annotation { "Feature Type Name" : "Feature", "Feature Type Description" : "" }
export const myFeature = defineFeature(function(context is Context, id is Id, definition is map)
    precondition{}
    {
        {
            var Q0;
            Q0=qCreatedBy(makeId("Top.planeOp"),FACE);
            var sketch = newSketch(context, id + "F0", { "sketchPlane" : qUnion([Q0])});
            skLineSegment(sketch, "E0.bottom", {"start": v(-51.86, 92.51) * mm, "end": v(-32.8, 92.51) * mm});
            skLineSegment(sketch, "E0.top", {"start": v(-51.86, -110.69) * mm, "end": v(-32.8, -110.69) * mm});
            skLineSegment(sketch, "E0.left", {"start": v(-51.86, 92.51) * mm, "end": v(-51.86, -110.69) * mm});
            skLineSegment(sketch, "E0.right", {"start": v(-32.8, 92.51) * mm, "end": v(-32.8, -110.69) * mm});
            skCircle(sketch, "E1", {"center": v(-42.33, 116.06) * mm, "radius": 25.4 * mm});
            skPoint(sketch, "E1.third.point", {"position": v(-42.33, 141.46) * mm});
            skPoint(sketch, "E1.third.point.positionSnap0", {"position": v(-42.33, 92.51) * mm});
            skCircle(sketch, "E2", {"center": v(-42.33, 116.06) * mm, "radius": 19.05 * mm});
            skLineSegment(sketch, "E3", {"start": v(-42.33, -110.69) * mm, "end": v(-32.8, -60.79) * mm});
            skLineSegment(sketch, "E4", {"start": v(-42.33, -110.69) * mm, "end": v(-51.86, -60.79) * mm});
            skSolve(sketch);
        }
        {
            var Q0;
            {var subQ6=sQuery(id+"F0.wireOp",EDGE,"E3");Q0=makeQuery(id+"F0.imprint","IMPRINT",FACE,{"disambiguationData":[TD([[makeQuery(id+"F0.imprint","IMPRINT",EDGE,{"derivedFrom":subQ6}),1.0]])]});}
            var Q1;
            {var subQ0=sQuery(id+"F0.wireOp",EDGE,"E0.bottom");Q1=makeQuery(id+"F0.imprint","IMPRINT",FACE,{"disambiguationData":[TD([[makeQuery(id+"F0.imprint","IMPRINT",EDGE,{"derivedFrom":subQ0}),-1.0]])]});}
            var Q2;
            {var subQ0=sQuery(id+"F0.wireOp",EDGE,"E0.bottom");Q2=makeQuery(id+"F0.imprint","IMPRINT",FACE,{"disambiguationData":[TD([[makeQuery(id+"F0.imprint","IMPRINT",EDGE,{"derivedFrom":subQ0}),1.0]])]});}
            extrude(context, id + "F1", {"entities" : qUnion([Q0, Q1, Q2]), "depth" : 3.17 * mm, "offsetDistance" : 25.4 * mm});
        }
        {
            var Q0;
            Q0=makeQuery(id+"F1.opExtrude","CAP_FACE",FACE,{"disambiguationData":[OSD([sQuery(id+"F0.wireOp",EDGE,"E0.left"),sQuery(id+"F0.wireOp",EDGE,"E0.right"),sQuery(id+"F0.wireOp",EDGE,"E1"),sQuery(id+"F0.wireOp",EDGE,"E2"),sQuery(id+"F0.wireOp",EDGE,"E3"),sQuery(id+"F0.wireOp",EDGE,"E4")])],"isStart":false});
            var sketch = newSketch(context, id + "F2", { "sketchPlane" : qUnion([Q0])});
            skLineSegment(sketch, "E5", {"start": v(-51.86, -60.79) * mm, "end": v(-32.8, -60.79) * mm});
            skLineSegment(sketch, "E6", {"start": v(-42.33, -110.69) * mm, "end": v(-43.92, -60.79) * mm});
            skLineSegment(sketch, "E7", {"start": v(-42.33, -110.69) * mm, "end": v(-40.74, -60.79) * mm});
            skPoint(sketch, "E8", {"position": v(-42.33, -60.79) * mm});
            skLineSegment(sketch, "E9", {"start": v(-51.86, 92.51) * mm, "end": v(-32.8, 92.51) * mm});
            skLineSegment(sketch, "E10.bottom", {"start": v(-43.92, -60.79) * mm, "end": v(-40.74, -60.79) * mm});
            skLineSegment(sketch, "E10.top", {"start": v(-43.92, 92.51) * mm, "end": v(-40.74, 92.51) * mm});
            skLineSegment(sketch, "E10.left", {"start": v(-43.92, -60.79) * mm, "end": v(-43.92, 92.51) * mm});
            skLineSegment(sketch, "E10.right", {"start": v(-40.74, -60.79) * mm, "end": v(-40.74, 92.51) * mm});
            skSolve(sketch);
        }
        {
            var Q0;
            Q0=makeQuery(id+"F2.imprint","IMPRINT",FACE,{"disambiguationData":[TD([[makeQuery(id+"F2.imprint","IMPRINT",EDGE,{"derivedFrom":sQuery(id+"F2.wireOp",EDGE,"E10.bottom")}),1.0]])]});
            var Q1;
            Q1=makeQuery(id+"F2.imprint","IMPRINT",FACE,{"disambiguationData":[TD([[makeQuery(id+"F2.imprint","IMPRINT",EDGE,{"derivedFrom":sQuery(id+"F2.wireOp",EDGE,"E6")}),-1.0]])]});
            extrude(context, id + "F3", {"entities" : qUnion([Q0, Q1]), "operationType" : NewBodyOperationType.ADD, "depth" : 12.7 * mm, "offsetDistance" : 25.4 * mm});
        }
        {
            var Q0;
            Q0=qCreatedBy(makeId("Right.planeOp"),FACE);
            var sketch = newSketch(context, id + "F4", { "sketchPlane" : qUnion([Q0])});
            skLineSegment(sketch, "E11.0.0", {"start": v(-60.79, 3.18) * mm, "end": v(92.51, 3.18) * mm});
            skLineSegment(sketch, "E11.0.1", {"start": v(92.51, 3.18) * mm, "end": v(92.51, 15.88) * mm});
            skLineSegment(sketch, "E11.0.2", {"start": v(92.51, 15.88) * mm, "end": v(-60.79, 15.88) * mm});
            skLineSegment(sketch, "E11.0.3", {"start": v(-60.79, 15.88) * mm, "end": v(-60.79, 3.18) * mm});
            skLineSegment(sketch, "E12.0.0", {"start": v(-110.69, 3.18) * mm, "end": v(-60.79, 3.18) * mm});
            skLineSegment(sketch, "E12.0.1", {"start": v(-60.79, 3.18) * mm, "end": v(-60.79, 15.88) * mm});
            skLineSegment(sketch, "E12.0.2", {"start": v(-60.79, 15.88) * mm, "end": v(-110.69, 15.88) * mm});
            skLineSegment(sketch, "E12.0.3", {"start": v(-110.69, 15.88) * mm, "end": v(-110.69, 3.18) * mm});
            skLineSegment(sketch, "E13", {"start": v(-60.79, 15.87) * mm, "end": v(-110.69, 3.17) * mm});
            skArc(sketch, "E14", {"start": v(92.51, 3.17) * mm, "mid": v(68.36, 12.43) * mm, "end": v(42.73, 15.87) * mm});
            skSolve(sketch);
        }
        {
            var Q0;
            Q0=makeQuery(id+"F4.imprint","IMPRINT",FACE,{"disambiguationData":[TD([[makeQuery(id+"F4.imprint","IMPRINT",EDGE,{"derivedFrom":sQuery(id+"F4.wireOp",EDGE,"E12.0.2")}),1.0]])]});
            var Q1;
            {var subQ0=sQuery(id+"F4.wireOp",EDGE,"E11.0.1");Q1=makeQuery(id+"F4.imprint","IMPRINT",FACE,{"disambiguationData":[TD([[makeQuery(id+"F4.imprint","IMPRINT",EDGE,{"derivedFrom":subQ0}),1.0]])]});}
            extrude(context, id + "F5", {"entities" : qUnion([Q0, Q1]), "operationType" : NewBodyOperationType.REMOVE, "oppositeDirection" : true, "depth" : 128.02 * mm, "offsetDistance" : 25.4 * mm});
        }
        {
            var Q0;
            Q0=makeQuery(id+"F1.opExtrude","CAP_FACE",FACE,{"disambiguationData":[OSD([sQuery(id+"F0.wireOp",EDGE,"E0.left"),sQuery(id+"F0.wireOp",EDGE,"E0.right"),sQuery(id+"F0.wireOp",EDGE,"E1"),sQuery(id+"F0.wireOp",EDGE,"E2"),sQuery(id+"F0.wireOp",EDGE,"E3"),sQuery(id+"F0.wireOp",EDGE,"E4")])],"isStart":true});
            var sketch = newSketch(context, id + "F6", { "sketchPlane" : qUnion([Q0])});
            skLineSegment(sketch, "E15.bottom", {"start": v(-20.1, -92.51) * mm, "end": v(-64.56, -92.51) * mm});
            skLineSegment(sketch, "E15.top", {"start": v(-20.1, -79.81) * mm, "end": v(-64.56, -79.81) * mm});
            skLineSegment(sketch, "E15.left", {"start": v(-20.1, -92.51) * mm, "end": v(-20.1, -79.81) * mm});
            skLineSegment(sketch, "E15.right", {"start": v(-64.56, -92.51) * mm, "end": v(-64.56, -79.81) * mm});
            skLineSegment(sketch, "E16.0.0", {"start": v(-32.8, -92.51) * mm, "end": v(-32.8, 60.79) * mm});
            skLineSegment(sketch, "E16.0.1", {"start": v(-32.8, 60.79) * mm, "end": v(-42.33, 110.69) * mm});
            skLineSegment(sketch, "E16.0.2", {"start": v(-42.33, 110.69) * mm, "end": v(-51.86, 60.79) * mm});
            skLineSegment(sketch, "E16.0.3", {"start": v(-51.86, 60.79) * mm, "end": v(-51.86, -92.51) * mm});
            skArc(sketch, "E16.0.4", {"start": v(-51.86, -92.51) * mm, "mid": v(-42.33, -141.46) * mm, "end": v(-32.8, -92.51) * mm});
            skSolve(sketch);
        }
        {
            var Q0;
            {var subQ3=sQuery(id+"F6.wireOp",EDGE,"E15.left");Q0=makeQuery(id+"F6.imprint","IMPRINT",FACE,{"disambiguationData":[TD([[makeQuery(id+"F6.imprint","IMPRINT",EDGE,{"derivedFrom":subQ3}),1.0]])]});}
            var Q1;
            {var subQ3=sQuery(id+"F6.wireOp",EDGE,"E15.right");Q1=makeQuery(id+"F6.imprint","IMPRINT",FACE,{"disambiguationData":[TD([[makeQuery(id+"F6.imprint","IMPRINT",EDGE,{"derivedFrom":subQ3}),-1.0]])]});}
            extrude(context, id + "F7", {"entities" : qUnion([Q0, Q1]), "operationType" : NewBodyOperationType.ADD, "oppositeDirection" : true, "depth" : 3.17 * mm, "offsetDistance" : 25.4 * mm});
        }
        {
            var Q0;
            Q0=makeQuery(id+"F1.opExtrude","SWEPT_BODY",BODY,{"disambiguationData":[OSD([sQuery(id+"F0.wireOp",EDGE,"E0.left"),sQuery(id+"F0.wireOp",EDGE,"E0.right"),sQuery(id+"F0.wireOp",EDGE,"E1"),sQuery(id+"F0.wireOp",EDGE,"E2"),sQuery(id+"F0.wireOp",EDGE,"E3"),sQuery(id+"F0.wireOp",EDGE,"E4")])]});
            var Q1;
            Q1=makeQuery(id+"F7.opExtrude","CAP_EDGE",EDGE,{"disambiguationData":[OSD([sQuery(id+"F6.wireOp",EDGE,"E15.left")])],"isStart":true});
            transform(context, id + "F8", {"entities" : qUnion([Q0]), "transformType" : TransformType.ROTATION, "transformAxis" : qUnion([Q1]), "angle" : 180 * degree, "makeCopy" : false});
        }
        {
            var Q0;
            {var subQ0=sQuery(id+"F6.wireOp",EDGE,"E15.top");var subQ1=sQuery(id+"F6.wireOp",EDGE,"E15.bottom");Q0=makeQuery(id+"F7.boolean.opBoolean","MERGE",FACE,{"derivedFrom":[makeQuery(id+"F1.opExtrude","CAP_FACE",FACE,{"disambiguationData":[OSD([sQuery(id+"F0.wireOp",EDGE,"E0.left"),sQuery(id+"F0.wireOp",EDGE,"E0.right"),sQuery(id+"F0.wireOp",EDGE,"E1"),sQuery(id+"F0.wireOp",EDGE,"E2"),sQuery(id+"F0.wireOp",EDGE,"E3"),sQuery(id+"F0.wireOp",EDGE,"E4")])],"isStart":true}),makeQuery(id+"F7.opExtrude","CAP_FACE",FACE,{"disambiguationData":[OSD([subQ1,subQ0,sQuery(id+"F6.wireOp",EDGE,"E15.left"),sQuery(id+"F6.wireOp",EDGE,"E16.0.0")])],"isStart":true}),makeQuery(id+"F7.opExtrude","CAP_FACE",FACE,{"disambiguationData":[OSD([subQ1,subQ0,sQuery(id+"F6.wireOp",EDGE,"E15.right"),sQuery(id+"F6.wireOp",EDGE,"E16.0.3")])],"isStart":true})]});}
            var sketch = newSketch(context, id + "F9", { "sketchPlane" : qUnion([Q0])});
            skText(sketch, "E17", { "text": "JMM BIO", "fontName": "OpenSans-Bold.ttf"});
            skPoint(sketch, "E18", {"position": v(-17.57, 89.97) * mm});
            const initialGuessF9  = {"E17": [-0.01757, 0.08347, 1, 0, 0.0065]};
            skSetInitialGuess(sketch, initialGuessF9);
            skSolve(sketch);
        }
        {
            var Q0;
            Q0=makeQuery(id+"F9.imprint","IMPRINT",FACE,{"disambiguationData":[TD([[makeQuery(id+"F9.imprint","IMPRINT",EDGE,{"derivedFrom":sQuery(id+"F9.wireOp",EDGE,"E17.sketch_text.stroke-0")}),-1.0]])]});
            var Q1;
            Q1=makeQuery(id+"F9.imprint","IMPRINT",FACE,{"disambiguationData":[TD([[makeQuery(id+"F9.imprint","IMPRINT",EDGE,{"derivedFrom":sQuery(id+"F9.wireOp",EDGE,"E17.sketch_text.stroke-10")}),-1.0]])]});
            var Q2;
            Q2=makeQuery(id+"F9.imprint","IMPRINT",FACE,{"disambiguationData":[TD([[makeQuery(id+"F9.imprint","IMPRINT",EDGE,{"derivedFrom":sQuery(id+"F9.wireOp",EDGE,"E17.sketch_text.stroke-29")}),-1.0]])]});
            var Q3;
            Q3=makeQuery(id+"F9.imprint","IMPRINT",FACE,{"disambiguationData":[TD([[makeQuery(id+"F9.imprint","IMPRINT",EDGE,{"derivedFrom":sQuery(id+"F9.wireOp",EDGE,"E17.sketch_text.stroke-48")}),-1.0]])]});
            var Q4;
            Q4=makeQuery(id+"F9.imprint","IMPRINT",FACE,{"disambiguationData":[TD([[makeQuery(id+"F9.imprint","IMPRINT",EDGE,{"derivedFrom":sQuery(id+"F9.wireOp",EDGE,"E17.sketch_text.stroke-73")}),-1.0]])]});
            var Q5;
            Q5=makeQuery(id+"F9.imprint","IMPRINT",FACE,{"disambiguationData":[TD([[makeQuery(id+"F9.imprint","IMPRINT",EDGE,{"derivedFrom":sQuery(id+"F9.wireOp",EDGE,"E17.sketch_text.stroke-77")}),-1.0]])]});
            extrude(context, id + "F10", {"entities" : qUnion([Q0, Q1, Q2, Q3, Q4, Q5]), "operationType" : NewBodyOperationType.REMOVE, "oppositeDirection" : true, "depth" : 1.59 * mm, "offsetDistance" : 25.4 * mm});
        }
    });